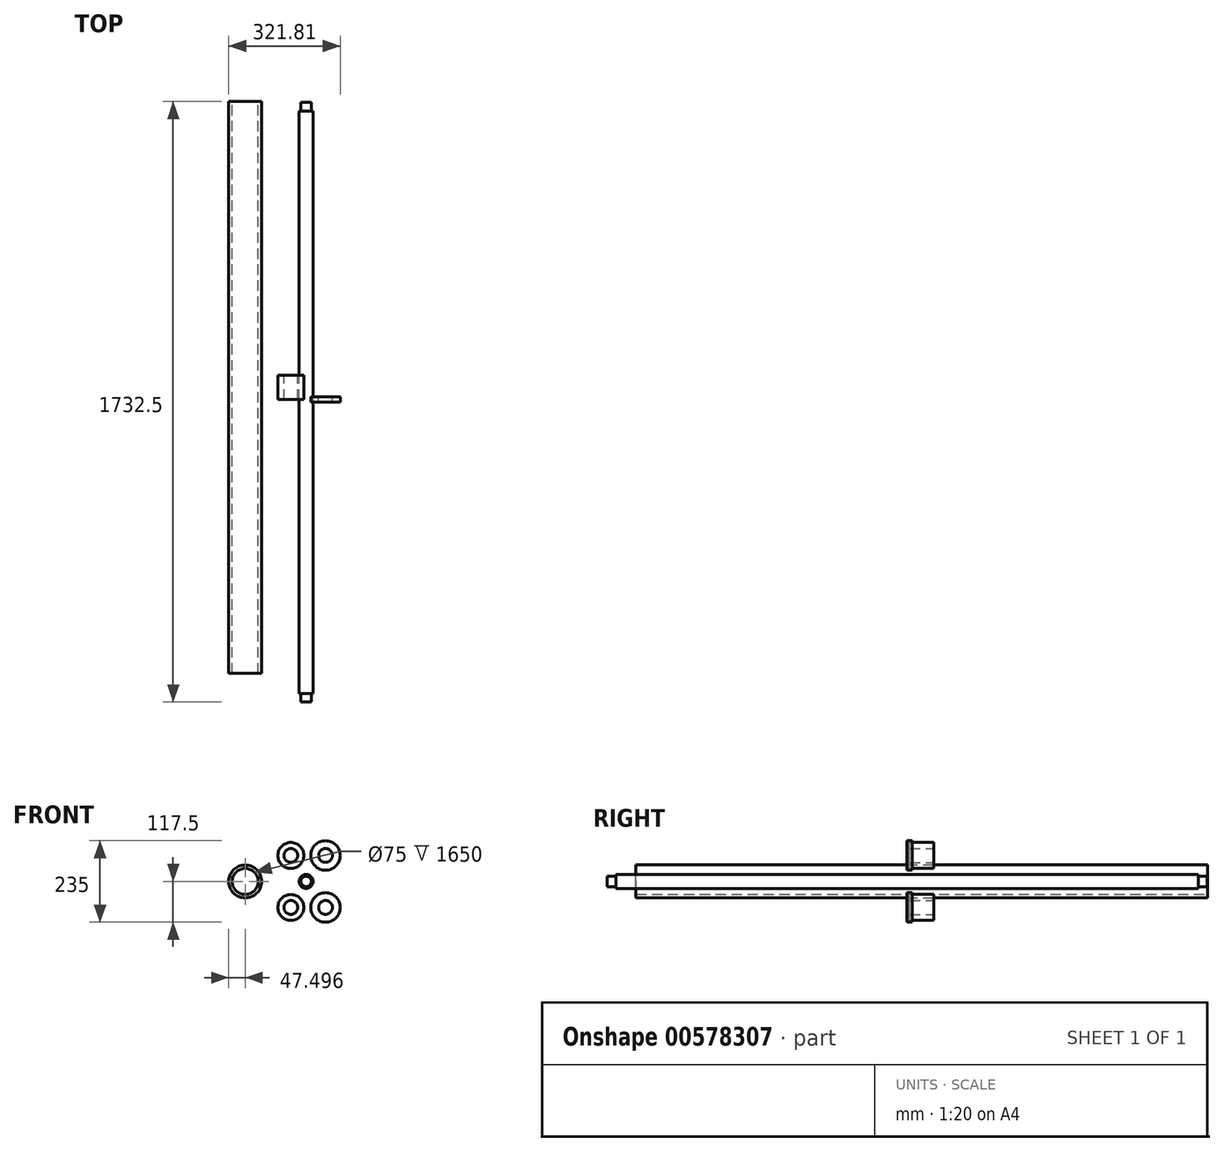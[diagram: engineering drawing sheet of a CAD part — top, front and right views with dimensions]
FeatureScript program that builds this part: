
annotation { "Feature Type Name" : "Feature", "Feature Type Description" : "" }
export const myFeature = defineFeature(function(context is Context, id is Id, definition is map)
    precondition{}
    {
        {
            var Q0;
            Q0=qCreatedBy(makeId("Front.planeOp"),FACE);
            var sketch = newSketch(context, id + "F0", { "sketchPlane" : qUnion([Q0])});
            skCircle(sketch, "E0", {"center": v(-56.81, 0) * mm, "radius": 47.5 * mm});
            skCircle(sketch, "E1", {"center": v(-56.81, 0) * mm, "radius": 37.5 * mm});
            skSolve(sketch);
        }
        {
            var Q0;
            Q0=makeQuery(id+"F0.imprint","IMPRINT",FACE,{"disambiguationData":[TD([[makeQuery(id+"F0.imprint","IMPRINT",EDGE,{"derivedFrom":sQuery(id+"F0.wireOp",EDGE,"E0")}),1.0]])]});
            extrude(context, id + "F1", {"entities" : qUnion([Q0]), "endBound" : BoundingType.SYMMETRIC, "depth" : 1650 * mm, "offsetDistance" : 25 * mm});
        }
        {
            var Q0;
            Q0=qCreatedBy(makeId("Front.planeOp"),FACE);
            var sketch = newSketch(context, id + "F2", { "sketchPlane" : qUnion([Q0])});
            skCircle(sketch, "E2", {"center": v(75, 75) * mm, "radius": 37.5 * mm});
            skCircle(sketch, "E3", {"center": v(75, 75) * mm, "radius": 20 * mm});
            skCircle(sketch, "E4", {"center": v(75, -75) * mm, "radius": 37.5 * mm});
            skCircle(sketch, "E5", {"center": v(75, -75) * mm, "radius": 20 * mm});
            skSolve(sketch);
        }
        {
            var Q0;
            Q0=makeQuery(id+"F2.imprint","IMPRINT",FACE,{"disambiguationData":[TD([[makeQuery(id+"F2.imprint","IMPRINT",EDGE,{"derivedFrom":sQuery(id+"F2.wireOp",EDGE,"E2")}),1.0]])]});
            var Q1;
            Q1=makeQuery(id+"F2.imprint","IMPRINT",FACE,{"disambiguationData":[TD([[makeQuery(id+"F2.imprint","IMPRINT",EDGE,{"derivedFrom":sQuery(id+"F2.wireOp",EDGE,"E4")}),1.0]])]});
            extrude(context, id + "F3", {"entities" : qUnion([Q0, Q1]), "endBound" : BoundingType.SYMMETRIC, "depth" : 70 * mm, "offsetDistance" : 25 * mm});
        }
        {
            var Q0;
            Q0=makeQuery(id+"F3.opExtrude","CAP_FACE",FACE,{"disambiguationData":[OSD([sQuery(id+"F2.wireOp",EDGE,"E2"),sQuery(id+"F2.wireOp",EDGE,"E3")])],"isStart":false});
            var sketch = newSketch(context, id + "F4", { "sketchPlane" : qUnion([Q0])});
            skCircle(sketch, "E6", {"center": v(175, 75) * mm, "radius": 42.5 * mm});
            skCircle(sketch, "E7", {"center": v(175, 75) * mm, "radius": 20 * mm});
            skCircle(sketch, "E8", {"center": v(175, -75) * mm, "radius": 42.5 * mm});
            skCircle(sketch, "E9", {"center": v(175, -75) * mm, "radius": 20 * mm});
            skSolve(sketch);
        }
        {
            var Q0;
            Q0=makeQuery(id+"F4.imprint","IMPRINT",FACE,{"disambiguationData":[TD([[makeQuery(id+"F4.imprint","IMPRINT",EDGE,{"derivedFrom":sQuery(id+"F4.wireOp",EDGE,"E6")}),1.0]])]});
            var Q1;
            Q1=makeQuery(id+"F4.imprint","IMPRINT",FACE,{"disambiguationData":[TD([[makeQuery(id+"F4.imprint","IMPRINT",EDGE,{"derivedFrom":sQuery(id+"F4.wireOp",EDGE,"E8")}),1.0]])]});
            extrude(context, id + "F5", {"entities" : qUnion([Q0, Q1]), "endBound" : BoundingType.SYMMETRIC, "depth" : 15 * mm, "offsetDistance" : 25 * mm});
        }
        {
            var Q0;
            Q0=makeQuery(id+"F5.opExtrude","CAP_FACE",FACE,{"disambiguationData":[OSD([sQuery(id+"F4.wireOp",EDGE,"E6"),sQuery(id+"F4.wireOp",EDGE,"E7")])],"isStart":false});
            var sketch = newSketch(context, id + "F6", { "sketchPlane" : qUnion([Q0])});
            skCircle(sketch, "E10", {"center": v(119, 0) * mm, "radius": 20 * mm});
            skSolve(sketch);
        }
        {
            var Q0;
            Q0=makeQuery(id+"F6.imprint","IMPRINT",FACE,{"disambiguationData":[TD([[makeQuery(id+"F6.imprint","IMPRINT",EDGE,{"derivedFrom":sQuery(id+"F6.wireOp",EDGE,"E10")}),1.0]])]});
            extrude(context, id + "F7", {"entities" : qUnion([Q0]), "endBound" : BoundingType.SYMMETRIC, "depth" : 1680 * mm, "offsetDistance" : 25 * mm});
        }
        {
            var Q0;
            Q0=makeQuery(id+"F7.opExtrude","CAP_FACE",FACE,{"disambiguationData":[OSD([sQuery(id+"F6.wireOp",EDGE,"E10")])],"isStart":false});
            var sketch = newSketch(context, id + "F8", { "sketchPlane" : qUnion([Q0])});
            skCircle(sketch, "E11.0.0", {"center": v(119, 0) * mm, "radius": 20 * mm});
            skCircle(sketch, "E12", {"center": v(119, 0) * mm, "radius": 15 * mm});
            skSolve(sketch);
        }
        {
            var Q0;
            Q0=makeQuery(id+"F8.imprint","IMPRINT",FACE,{"disambiguationData":[TD([[makeQuery(id+"F8.imprint","IMPRINT",EDGE,{"derivedFrom":sQuery(id+"F8.wireOp",EDGE,"E12")}),1.0]])]});
            extrude(context, id + "F9", {"entities" : qUnion([Q0]), "operationType" : NewBodyOperationType.ADD, "depth" : 25 * mm, "offsetDistance" : 25 * mm});
        }
        {
            var Q0;
            Q0=makeQuery(id+"F7.opExtrude","CAP_FACE",FACE,{"disambiguationData":[OSD([sQuery(id+"F6.wireOp",EDGE,"E10")])],"isStart":true});
            var sketch = newSketch(context, id + "F10", { "sketchPlane" : qUnion([Q0])});
            skCircle(sketch, "E13.0.0", {"center": v(-119, 0) * mm, "radius": 20 * mm});
            skCircle(sketch, "E14", {"center": v(-119, 0) * mm, "radius": 15 * mm});
            skSolve(sketch);
        }
        {
            var Q0;
            Q0=makeQuery(id+"F10.imprint","IMPRINT",FACE,{"disambiguationData":[TD([[makeQuery(id+"F10.imprint","IMPRINT",EDGE,{"derivedFrom":sQuery(id+"F10.wireOp",EDGE,"E14")}),1.0]])]});
            extrude(context, id + "F11", {"entities" : qUnion([Q0]), "operationType" : NewBodyOperationType.ADD, "depth" : 25 * mm, "offsetDistance" : 25 * mm});
        }
    });
